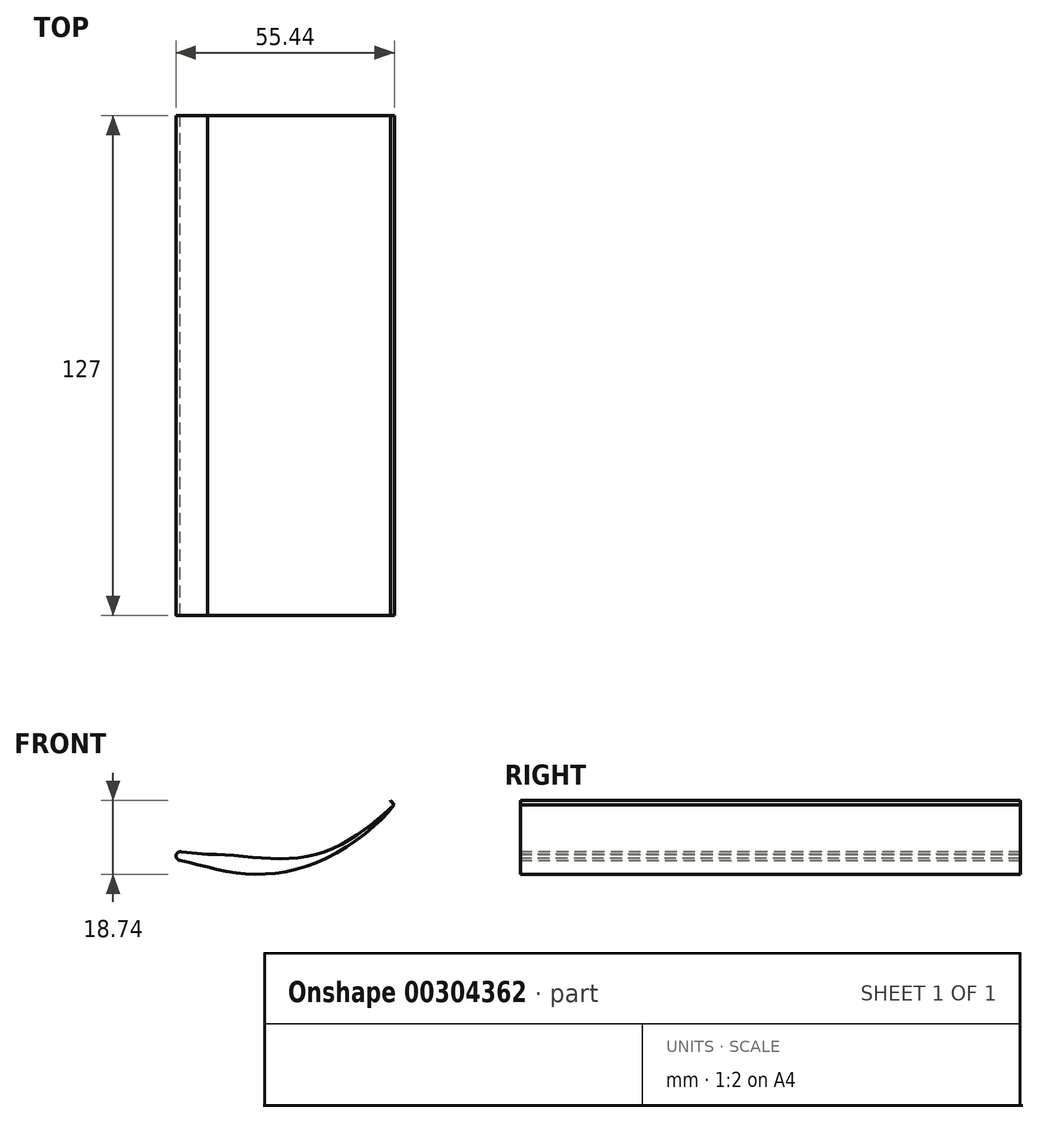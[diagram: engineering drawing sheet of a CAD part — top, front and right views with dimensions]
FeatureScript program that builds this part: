
annotation { "Feature Type Name" : "Feature", "Feature Type Description" : "" }
export const myFeature = defineFeature(function(context is Context, id is Id, definition is map)
    precondition{}
    {
        {
            var Q0;
            Q0=qCreatedBy(makeId("Front.planeOp"),FACE);
            var sketch = newSketch(context, id + "F0", { "sketchPlane" : qUnion([Q0])});
            skLineSegment(sketch, "E0", {"start": v(-64.75, -13.08) * mm, "end": v(-57.9, -13.75) * mm});
            skPoint(sketch, "E1", {"position": v(-12.06, -1.8) * mm});
            skArc(sketch, "E2", {"start": v(-64.75, -13.08) * mm, "mid": v(-65.96, -14.1) * mm, "end": v(-64.92, -15.28) * mm});
            skFitSpline(sketch, "E3", {"points": [v(-57.9, -13.75) * mm, v(-30.6, -13.85) * mm, v(-10.57, -1.22) * mm], "startDerivative": vector(49.79, 0.28) * mm, "endDerivative": vector(27.37, 25.53) * mm});
            skFitSpline(sketch, "E4", {"points": [v(-10.57, -1.22) * mm, v(-28.03, -14.85) * mm, v(-47.84, -18.73) * mm, v(-64.92, -15.28) * mm], "startDerivative": vector(-29.94, -40.57) * mm, "endDerivative": vector(-51.28, 12.54) * mm});
            skSolve(sketch);
        }
        {
            var Q0;
            Q0=makeQuery(id+"F0.imprint","IMPRINT",FACE,{"disambiguationData":[TD([[makeQuery(id+"F0.imprint","IMPRINT",EDGE,{"derivedFrom":sQuery(id+"F0.wireOp",EDGE,"E0")}),-1.0]])]});
            extrude(context, id + "F1", {"entities" : qUnion([Q0]), "endBound" : BoundingType.SYMMETRIC, "depth" : 127 * mm});
        }
        {
            var Q0;
            Q0=qCreatedBy(makeId("Front.planeOp"),FACE);
            var sketch = newSketch(context, id + "F2", { "sketchPlane" : qUnion([Q0])});
            skLineSegment(sketch, "E5", {"start": v(-10.62, -1.24) * mm, "end": v(-11.43, -0.15) * mm});
            skLineSegment(sketch, "E6", {"start": v(-11.43, -0.15) * mm, "end": v(-11.43, -0.08) * mm});
            skLineSegment(sketch, "E7", {"start": v(-11.43, -0.08) * mm, "end": v(-10.52, -1.22) * mm});
            skLineSegment(sketch, "E8", {"start": v(-10.52, -1.22) * mm, "end": v(-10.62, -1.24) * mm});
            skSolve(sketch);
        }
        {
            var Q0;
            Q0=makeQuery(id+"F2.imprint","IMPRINT",FACE,{"disambiguationData":[TD([[makeQuery(id+"F2.imprint","IMPRINT",EDGE,{"derivedFrom":sQuery(id+"F2.wireOp",EDGE,"E5")}),-1.0]])]});
            extrude(context, id + "F3", {"entities" : qUnion([Q0]), "operationType" : NewBodyOperationType.ADD, "endBound" : BoundingType.SYMMETRIC, "depth" : 127 * mm});
        }
    });
